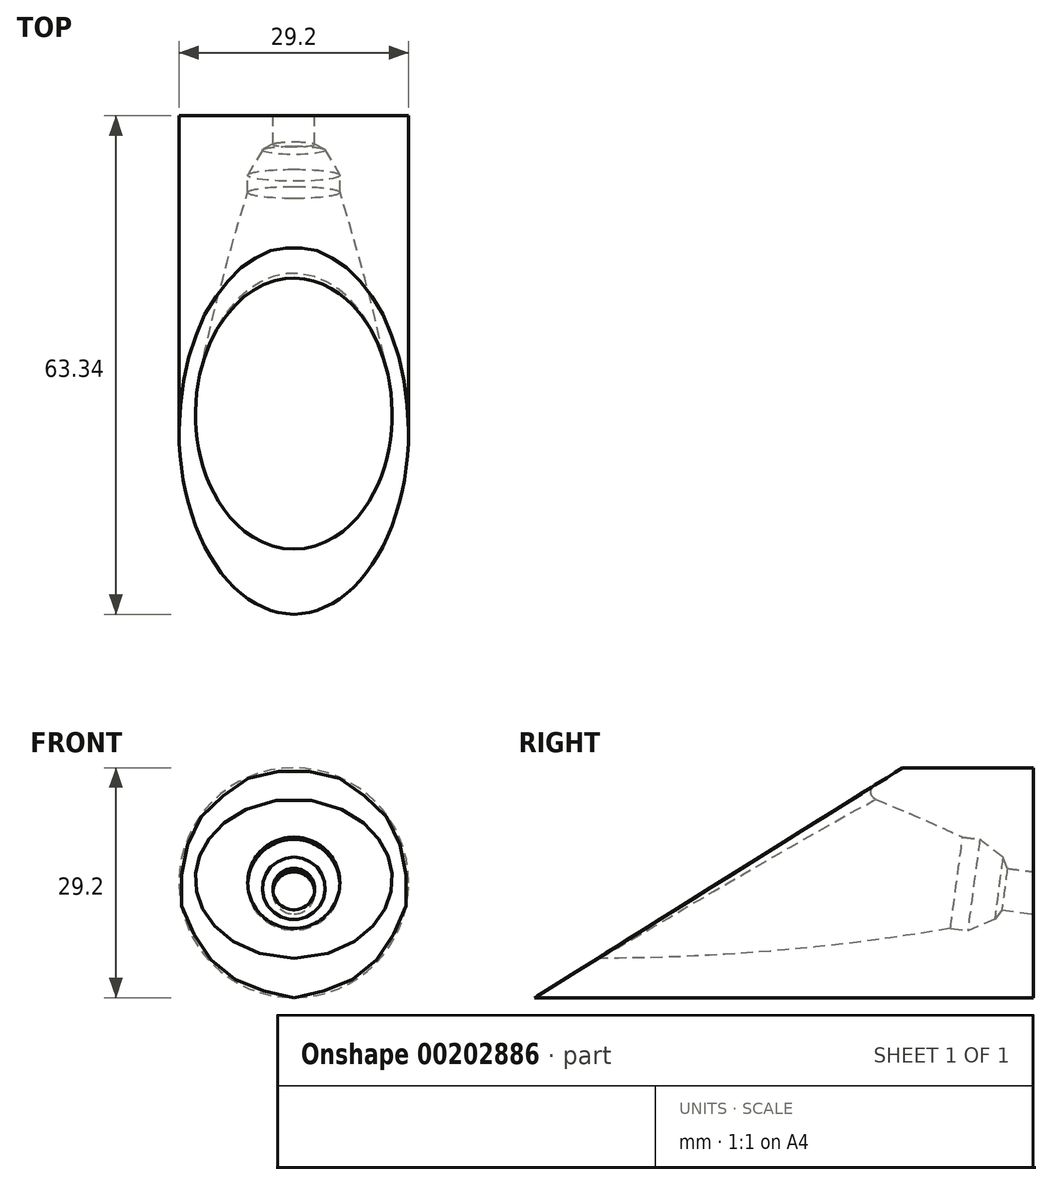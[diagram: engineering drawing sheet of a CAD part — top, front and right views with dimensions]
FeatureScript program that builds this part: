
annotation { "Feature Type Name" : "Feature", "Feature Type Description" : "" }
export const myFeature = defineFeature(function(context is Context, id is Id, definition is map)
    precondition{}
    {
        {
            var Q0;
            Q0=qCreatedBy(makeId("Front.planeOp"),FACE);
            var sketch = newSketch(context, id + "F0", { "sketchPlane" : qUnion([Q0])});
            skCircle(sketch, "E0", {"center": v(0, 0) * mm, "radius": 14.6 * mm});
            skLineSegment(sketch, "E1", {"start": v(-31.93, 0) * mm, "end": v(31.37, 0) * mm, "construction": true});
            skSolve(sketch);
        }
        {
            var Q0;
            Q0 = qSketchRegion(id + "F0", true);
            extrude(context, id + "F1", {"entities" : qUnion([Q0]), "oppositeDirection" : true, "depth" : 65 * mm});
        }
        {
            var Q0;
            Q0=sQuery(id+"F0.wireOp",EDGE,"E1");
            var Q1;
            Q1=qCreatedBy(makeId("Front.planeOp"),FACE);
            cPlane(context, id + "F2", {"entities" : qUnion([Q0, Q1]), "cplaneType" : CPlaneType.LINE_ANGLE, "offset" : 25 * mm, "angle" : 32 * degree, "width" : 150 * mm, "height" : 150 * mm});
        }
        {
            var Q0;
            Q0=qCreatedBy(id+"F2.planeOp",FACE);
            var sketch = newSketch(context, id + "F3", { "sketchPlane" : qUnion([Q0])});
            skLineSegment(sketch, "E2", {"start": v(0, 16.94) * mm, "end": v(0, -16.02) * mm, "construction": true});
            skSolve(sketch);
        }
        {
            var Q0;
            Q0=sQuery(id+"F3.wireOp",EDGE,"E2");
            var Q1;
            Q1=qCreatedBy(id+"F2.planeOp",FACE);
            cPlane(context, id + "F4", {"entities" : qUnion([Q0, Q1]), "cplaneType" : CPlaneType.LINE_ANGLE, "offset" : 25 * mm, "angle" : 5 * degree, "width" : 150 * mm, "height" : 150 * mm});
        }
        {
            var Q0;
            Q0=qCreatedBy(id+"F4.planeOp",FACE);
            cPlane(context, id + "F5", {"entities" : qUnion([Q0]), "cplaneType" : CPlaneType.OFFSET, "offset" : 14 * mm, "width" : 150 * mm, "height" : 150 * mm});
        }
        {
            var Q0;
            Q0=qCreatedBy(id+"F5.planeOp",FACE);
            var sketch = newSketch(context, id + "F6", { "sketchPlane" : qUnion([Q0])});
            skLineSegment(sketch, "E3.bottom", {"start": v(22.5, 13.26) * mm, "end": v(-22.5, 13.26) * mm});
            skLineSegment(sketch, "E3.top", {"start": v(22.5, -13.26) * mm, "end": v(-22.5, -13.26) * mm});
            skLineSegment(sketch, "E3.left", {"start": v(22.5, 13.26) * mm, "end": v(22.5, -13.26) * mm});
            skLineSegment(sketch, "E3.right", {"start": v(-22.5, 13.26) * mm, "end": v(-22.5, -13.26) * mm});
            skPoint(sketch, "E3.middle", {"position": v(0, 0) * mm});
            skEllipse(sketch, "E4.0", {"center": v(0, 0) * mm, "majorRadius": 15.2 * mm, "minorRadius": 12.84 * mm, "majorAxis": v(1, -0.14), "construction": true});
            skSolve(sketch);
        }
        {
            var Q0;
            Q0=makeQuery(id+"F6.imprint","IMPRINT",FACE,{"disambiguationData":[TD([[makeQuery(id+"F6.imprint","IMPRINT",EDGE,{"derivedFrom":sQuery(id+"F6.wireOp",EDGE,"E3.bottom")}),1.0]])]});
            extrude(context, id + "F7", {"entities" : qUnion([Q0]), "operationType" : NewBodyOperationType.REMOVE, "endBound" : BoundingType.THROUGH_ALL, "oppositeDirection" : true, "depth" : 25 * mm});
        }
        {
            var Q0;
            Q0=qCreatedBy(makeId("Right.planeOp"),FACE);
            var sketch = newSketch(context, id + "F8", { "sketchPlane" : qUnion([Q0])});
            skLineSegment(sketch, "E5.0", {"start": v(48.4, 14.6) * mm, "end": v(30.31, 3.3) * mm, "construction": true});
            skLineSegment(sketch, "E6.0", {"start": v(65, -14.6) * mm, "end": v(65, 14.6) * mm, "construction": true});
            skLineSegment(sketch, "E7", {"start": v(48.4, 14.6) * mm, "end": v(65, 14.6) * mm, "construction": true});
            skLineSegment(sketch, "E8", {"start": v(65, -14.6) * mm, "end": v(1.66, -14.6) * mm, "construction": true});
            skLineSegment(sketch, "E9", {"start": v(30.31, 3.3) * mm, "end": v(1.66, -14.6) * mm, "construction": true});
            skLineSegment(sketch, "E10", {"start": v(30.31, 3.3) * mm, "end": v(65, -1.3) * mm, "construction": true});
            skLineSegment(sketch, "E11", {"start": v(65.35, -1.34) * mm, "end": v(65, -3.96) * mm});
            skLineSegment(sketch, "E12", {"start": v(65, -3.96) * mm, "end": v(61, -3.43) * mm});
            skLineSegment(sketch, "E13", {"start": v(61, -3.43) * mm, "end": v(60.08, -4.67) * mm});
            skLineSegment(sketch, "E14", {"start": v(60.08, -4.67) * mm, "end": v(56.66, -6.09) * mm});
            skLineSegment(sketch, "E15", {"start": v(56.66, -6.09) * mm, "end": v(54.48, -5.8) * mm});
            skLineSegment(sketch, "E16", {"start": v(54.48, -5.8) * mm, "end": v(55.25, 0) * mm, "construction": true});
            skLineSegment(sketch, "E17", {"start": v(55.25, 0) * mm, "end": v(65.35, -1.34) * mm});
            skLineSegment(sketch, "E18", {"start": v(60.08, -4.67) * mm, "end": v(60.6, -0.7) * mm, "construction": true});
            skLineSegment(sketch, "E19", {"start": v(61, -3.43) * mm, "end": v(61.35, -0.8) * mm, "construction": true});
            skLineSegment(sketch, "E20", {"start": v(56.66, -6.09) * mm, "end": v(57.43, -0.29) * mm, "construction": true});
            skPoint(sketch, "E21", {"position": v(65, 0) * mm});
            skArc(sketch, "E22", {"start": v(9.66, -9.6) * mm, "mid": v(32.15, -8.65) * mm, "end": v(54.48, -5.8) * mm});
            skLineSegment(sketch, "E23.0", {"start": v(65, -9.6) * mm, "end": v(1.66, -9.6) * mm, "construction": true});
            skArc(sketch, "E24.MirrorCS", {"start": v(13.73, 21.14) * mm, "mid": v(35.2, 14.36) * mm, "end": v(56.02, 5.8) * mm, "construction": true});
            skLineSegment(sketch, "E25.MirrorCS", {"start": v(58.2, 5.51) * mm, "end": v(56.02, 5.8) * mm, "construction": true});
            skLineSegment(sketch, "E26.MirrorCS", {"start": v(61.13, 3.26) * mm, "end": v(58.2, 5.51) * mm, "construction": true});
            skLineSegment(sketch, "E27.MirrorCS", {"start": v(61.7, 1.82) * mm, "end": v(61.13, 3.26) * mm, "construction": true});
            skLineSegment(sketch, "E28.MirrorCS", {"start": v(65.7, 1.29) * mm, "end": v(61.7, 1.82) * mm, "construction": true});
            skLineSegment(sketch, "E29.MirrorCS", {"start": v(65.35, -1.34) * mm, "end": v(65.7, 1.29) * mm, "construction": true});
            skPoint(sketch, "E30", {"position": v(43.16, 11.33) * mm});
            skLineSegment(sketch, "E31", {"start": v(9.66, -9.6) * mm, "end": v(11.7, 5.77) * mm});
            skLineSegment(sketch, "E32", {"start": v(11.7, 5.77) * mm, "end": v(65.35, -1.34) * mm});
            skSolve(sketch);
        }
        {
            var Q0;
            Q0 = qSketchRegion(id + "F8", true);
            var Q1;
            Q1=sQuery(id+"F8.wireOp",EDGE,"E10");
            revolve(context, id + "F9", {"operationType" : NewBodyOperationType.REMOVE, "entities" : qUnion([Q0]), "axis" : qUnion([Q1]), "revolveType" : RevolveType.FULL, "oppositeDirection" : true});
        }
        {
            var Q0;
            Q0=makeQuery(id+"F9.boolean.opBoolean","INTERSECT",EDGE,{"derivedFrom":[makeQuery(id+"F7.boolean.opBoolean","COPY",FACE,{"derivedFrom":makeQuery(id+"F7.opExtrude","SWEPT_FACE",FACE,{"disambiguationData":[OSD([sQuery(id+"F6.wireOp",EDGE,"E3.top")])]})}),makeQuery(id+"F9.opRevolve","SWEPT_FACE",FACE,{"disambiguationData":[OSD([sQuery(id+"F8.wireOp",EDGE,"E22")])]})]});
            fillet(context, id + "F10", {"entities" : qUnion([Q0]), "radius" : 1 * mm, "tangentPropagation" : true, "allowEdgeOverflow" : false});
        }
    });
